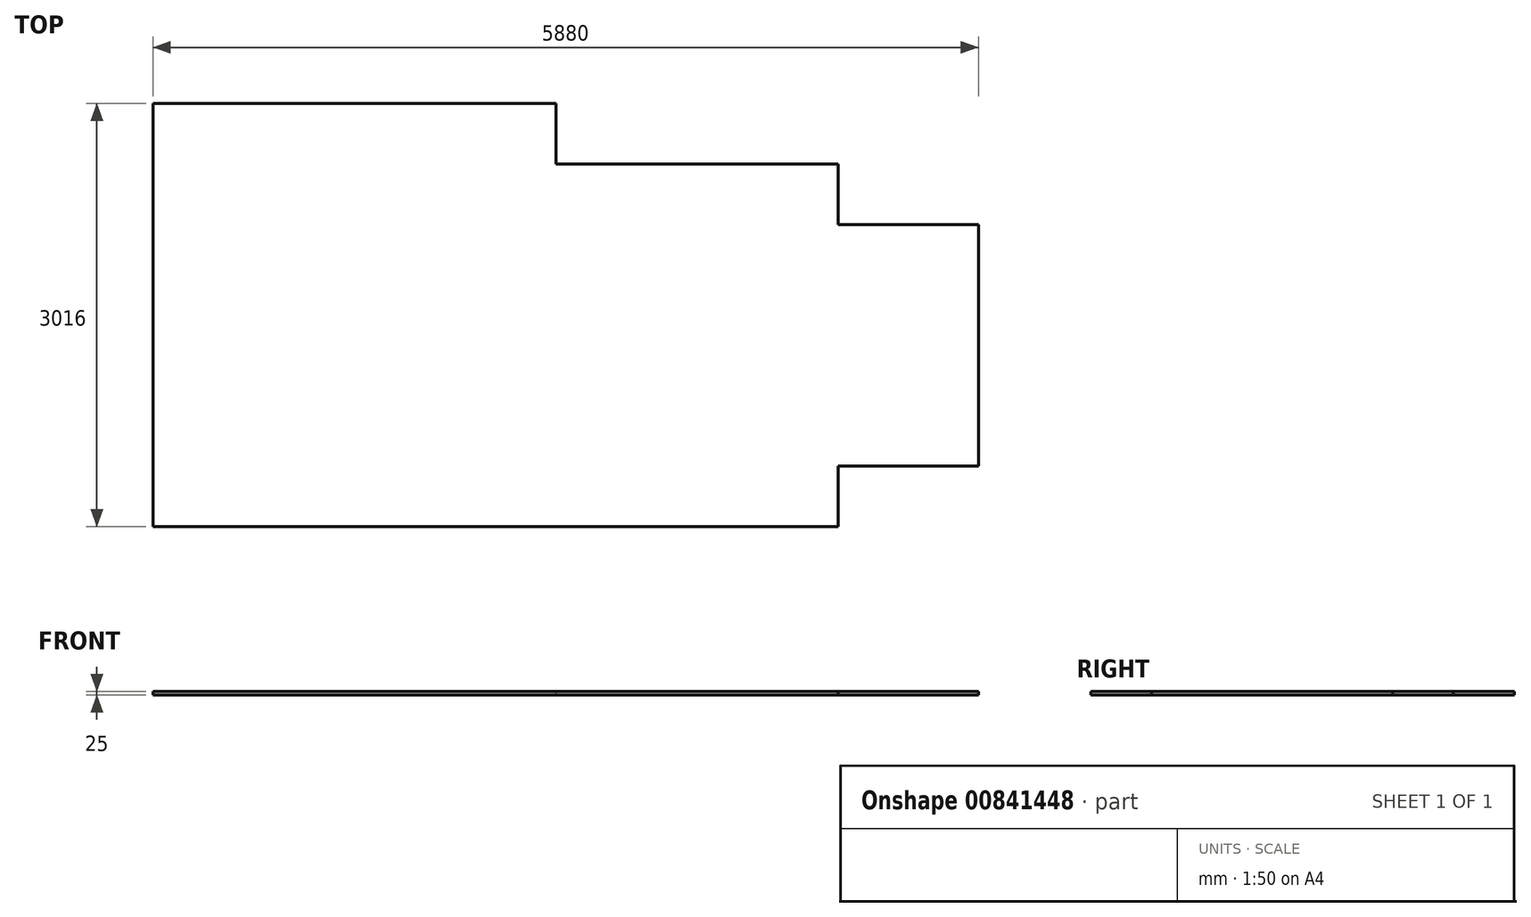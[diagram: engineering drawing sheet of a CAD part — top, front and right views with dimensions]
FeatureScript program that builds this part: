
annotation { "Feature Type Name" : "Feature", "Feature Type Description" : "" }
export const myFeature = defineFeature(function(context is Context, id is Id, definition is map)
    precondition{}
    {
        {
            var Q0;
            Q0=qCreatedBy(makeId("Top.planeOp"),FACE);
            var sketch = newSketch(context, id + "F0", { "sketchPlane" : qUnion([Q0])});
            skLineSegment(sketch, "E0", {"start": v(0, 0) * mm, "end": v(4880, 0) * mm});
            skLineSegment(sketch, "E1", {"start": v(4880, 0) * mm, "end": v(4880, 432) * mm});
            skLineSegment(sketch, "E2", {"start": v(4880, 432) * mm, "end": v(5880, 432) * mm});
            skLineSegment(sketch, "E3", {"start": v(5880, 432) * mm, "end": v(5880, 2152) * mm});
            skLineSegment(sketch, "E4", {"start": v(5880, 2152) * mm, "end": v(4880, 2152) * mm});
            skLineSegment(sketch, "E5", {"start": v(4880, 2152) * mm, "end": v(4880, 2584) * mm});
            skLineSegment(sketch, "E6", {"start": v(4880, 2584) * mm, "end": v(2872, 2584) * mm});
            skLineSegment(sketch, "E7", {"start": v(2872, 2584) * mm, "end": v(2872, 3016) * mm});
            skLineSegment(sketch, "E8", {"start": v(2872, 3016) * mm, "end": v(0, 3016) * mm});
            skLineSegment(sketch, "E9", {"start": v(0, 3016) * mm, "end": v(0, 0) * mm});
            skSolve(sketch);
        }
        {
            var Q0;
            Q0 = qSketchRegion(id + "F0", true);
            extrude(context, id + "F1", {"entities" : qUnion([Q0]), "oppositeDirection" : true, "depth" : 25 * mm, "offsetDistance" : 25 * mm});
        }
    });
